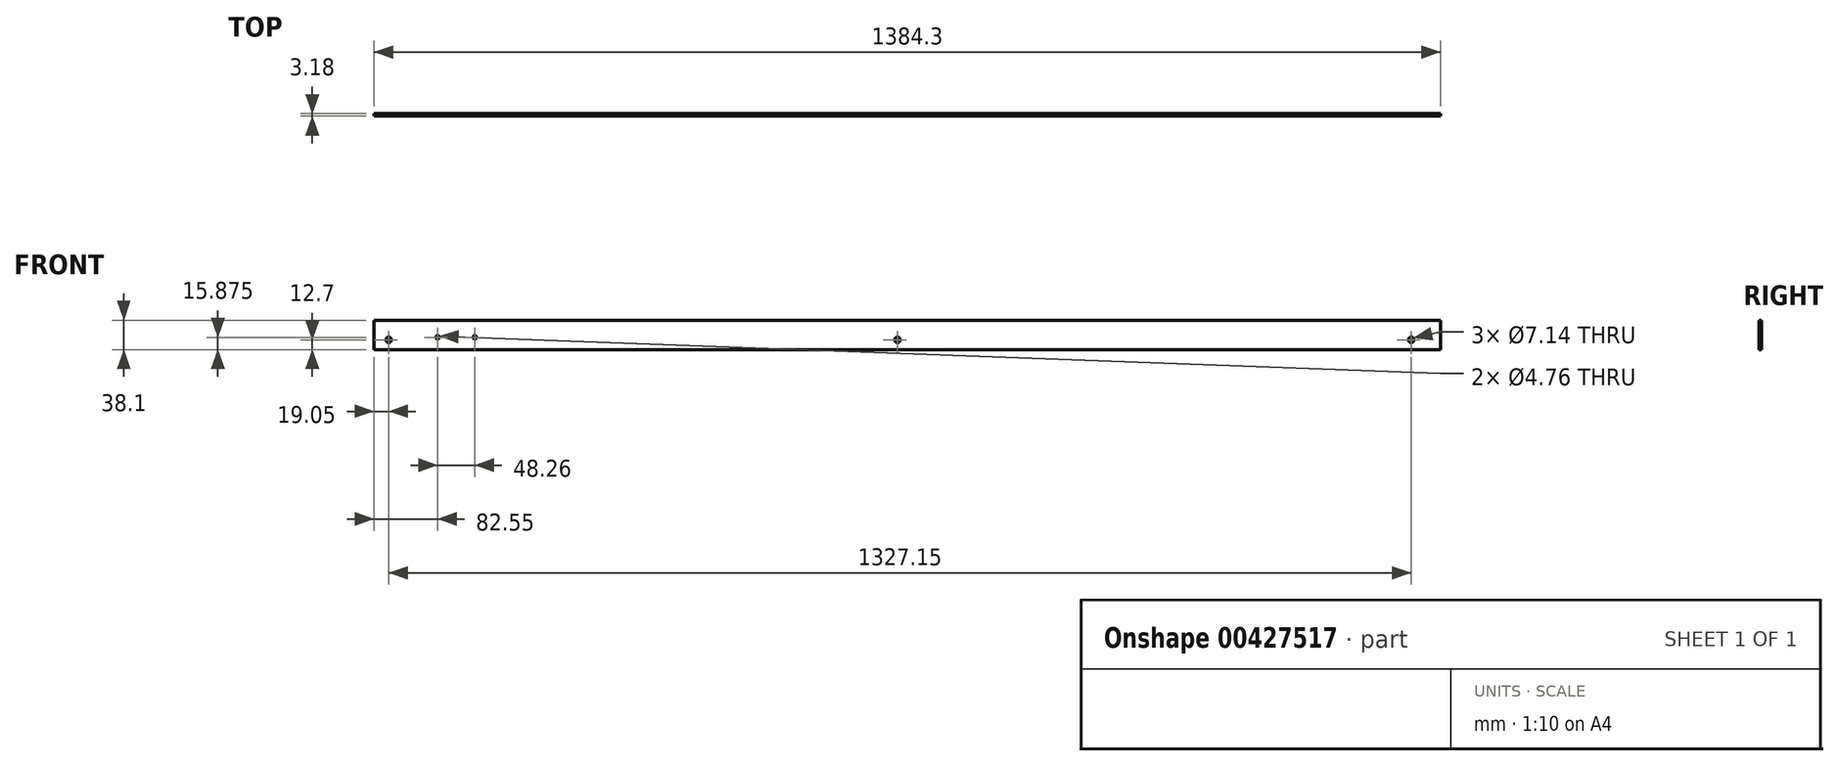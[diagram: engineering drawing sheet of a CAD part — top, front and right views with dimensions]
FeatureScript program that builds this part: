
annotation { "Feature Type Name" : "Feature", "Feature Type Description" : "" }
export const myFeature = defineFeature(function(context is Context, id is Id, definition is map)
    precondition{}
    {
        {
            var Q0;
            Q0=qCreatedBy(makeId("Front.planeOp"),FACE);
            var sketch = newSketch(context, id + "F0", { "sketchPlane" : qUnion([Q0])});
            skLineSegment(sketch, "E0.bottom", {"start": v(0, 0) * mm, "end": v(1384.3, 0) * mm});
            skLineSegment(sketch, "E0.top", {"start": v(0, 38.1) * mm, "end": v(1384.3, 38.1) * mm});
            skLineSegment(sketch, "E0.left", {"start": v(0, 0) * mm, "end": v(0, 38.1) * mm});
            skLineSegment(sketch, "E0.right", {"start": v(1384.3, 0) * mm, "end": v(1384.3, 38.1) * mm});
            skSolve(sketch);
        }
        {
            var Q0;
            Q0=makeQuery(id+"F0.imprint","IMPRINT",FACE,{"disambiguationData":[TD([[makeQuery(id+"F0.imprint","IMPRINT",EDGE,{"derivedFrom":sQuery(id+"F0.wireOp",EDGE,"E0.bottom")}),1.0]])]});
            extrude(context, id + "F1", {"entities" : qUnion([Q0]), "oppositeDirection" : true, "depth" : 3.17 * mm});
        }
        {
            var Q0;
            Q0=makeQuery(id+"F1.opExtrude","CAP_FACE",FACE,{"disambiguationData":[OSD([sQuery(id+"F0.wireOp",EDGE,"E0.bottom"),sQuery(id+"F0.wireOp",EDGE,"E0.top"),sQuery(id+"F0.wireOp",EDGE,"E0.left"),sQuery(id+"F0.wireOp",EDGE,"E0.right")])],"isStart":true});
            var sketch = newSketch(context, id + "F2", { "sketchPlane" : qUnion([Q0])});
            skCircle(sketch, "E1", {"center": v(19.05, 12.7) * mm, "radius": 3.57 * mm});
            skCircle(sketch, "E2", {"center": v(679.45, 12.7) * mm, "radius": 3.57 * mm});
            skCircle(sketch, "E3", {"center": v(1346.2, 12.7) * mm, "radius": 3.57 * mm});
            skCircle(sketch, "E4", {"center": v(82.55, 15.88) * mm, "radius": 2.38 * mm});
            skCircle(sketch, "E5", {"center": v(130.8, 15.88) * mm, "radius": 2.38 * mm});
            skSolve(sketch);
        }
        {
            var Q0;
            Q0=makeQuery(id+"F2.imprint","IMPRINT",FACE,{"disambiguationData":[TD([[makeQuery(id+"F2.imprint","IMPRINT",EDGE,{"derivedFrom":sQuery(id+"F2.wireOp",EDGE,"E1")}),1.0]])]});
            var Q1;
            Q1=makeQuery(id+"F2.imprint","IMPRINT",FACE,{"disambiguationData":[TD([[makeQuery(id+"F2.imprint","IMPRINT",EDGE,{"derivedFrom":sQuery(id+"F2.wireOp",EDGE,"E4")}),1.0]])]});
            var Q2;
            Q2=makeQuery(id+"F2.imprint","IMPRINT",FACE,{"disambiguationData":[TD([[makeQuery(id+"F2.imprint","IMPRINT",EDGE,{"derivedFrom":sQuery(id+"F2.wireOp",EDGE,"E5")}),1.0]])]});
            var Q3;
            Q3=makeQuery(id+"F2.imprint","IMPRINT",FACE,{"disambiguationData":[TD([[makeQuery(id+"F2.imprint","IMPRINT",EDGE,{"derivedFrom":sQuery(id+"F2.wireOp",EDGE,"E2")}),1.0]])]});
            var Q4;
            Q4=makeQuery(id+"F2.imprint","IMPRINT",FACE,{"disambiguationData":[TD([[makeQuery(id+"F2.imprint","IMPRINT",EDGE,{"derivedFrom":sQuery(id+"F2.wireOp",EDGE,"E3")}),1.0]])]});
            extrude(context, id + "F3", {"entities" : qUnion([Q0, Q1, Q2, Q3, Q4]), "operationType" : NewBodyOperationType.REMOVE, "endBound" : BoundingType.THROUGH_ALL, "oppositeDirection" : true, "depth" : 25.4 * mm});
        }
    });
